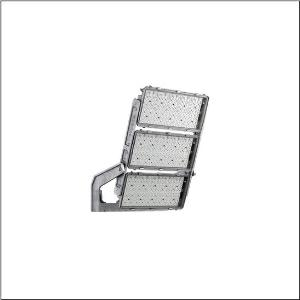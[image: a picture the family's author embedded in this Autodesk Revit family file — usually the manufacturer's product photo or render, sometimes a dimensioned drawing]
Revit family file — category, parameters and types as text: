
# Revit family: floodlight_fl_11_maxi_pro_remote___pl52_5xa779426d01aa_14f9
name_source: partatom
category: Lighting Fixtures
units: mm (PartAtom-declared; Revit-internal decimal feet)

## family parameters
Cut with Voids When Loaded = No
Host = Face
Light Source = No
Part Type = Normal
Room Calculation Point = No
Round Connector Dimension = Use Diameter
Shared = No

## types (1)
- --- (1 x LED, 169140 lm, 1387.6 W, 4000K)
    Apparent Load = 1388 VA
    CIE Flux Codes = 24 55 98 100 100
    Color Rendering = 70
    Color Temperature = 4000K
    Default Elevation = 1800 mm
    Description = Floodlight FL 11  maxi  pro Remote floodlight; light control with lens of PMMA; cover panel of toughened safety glass, transparent; light distribution: PL52, asymmetric direct distribution, LEDcolour temperature: 4000K, rated luminous flux: 169.140lm, colour rendering: CRI > 70, light colour: 740; luminous efficacy: 122lm/W; brightness control: DALI 2 (1 DALI address); with terminal, 8-pole, max. 2.5mm², mains connection: 220..240V/380..400V AC, 50/60Hz, surge voltage resistance: line to ground: 10kV, ECG replaceable separately, LED unit replaceable without ESD environment, dustproof LED module, dimming range 10..100%, no afterglow with DALI off / DMX off command; 1388W floodlight with 3x LED unit of diecast aluminium, coated grey; length: 713mm / width: 651mm / height: 338mm; mounting bracket, of diecast aluminium, uncoated, natural, equipment: Power, protection rating (complete): IP66; insulation class (complete): insulation class I (protective earthing); certification: CE, ENEC, VDE; ball protection: ball impact resistance with accessories, impact resistance: IK07; rated ambient temperature 10°C, only for outdoor installations, permissible operating ambient temperature: -40..+30°C, permissible storage temperature: -40..+85°C; packaging unit: 1 piece

Light Distribution: PL52
    Height = 320 mm
    Lamp = 1 x LED
    Lamp Light Flux = 169140 lm
    Lamp Power = 1387.6 W
    Lamp count = 1
    Length = 1002 mm
    Luminous efficacy = 122 lm/W
    Manufacturer = Siteco
    ModVariant = No
    Model = 5XA779426D01AA
    Mounting Place = Ceiling
    Mounting Type = Surface mounted
    Number of Poles = 1
    OnlyDefault = Yes
    Power Factor = 1
    Product Name = Floodlight FL 11 maxi pro Remote | PL52
    Product group = floodlight | ceiling mounted
    ProductGroupID = 302
    Protection Class = Protection class I
    Protection Degree = IP 66
    RLX_Detail_Level = 1
    RLX_Emergency_Light_Flux = 0 lm
    RLX_Emergency_Type = 0
    RLX_Emergency_Type_DB = No
    RlxData = <blob elided: 52421 chars, md5=a9be0326>
    Socket = socket
    Standby Power = 0 W
    System Light Flux = 169140 lm
    System Power = 1388 W
    Type Comments = factory setting: luminous flux: 100 % | dim-lin: 254 | 955 mA
    Type Image = l_1006784.jpg
    URL = http://relux.com
    VarID = @adj_028191
    Voltage = 0 V
    Weight = 0.00 kg
    Width = 655 mm

## geometry (parser evidence)
native form markers: Blend x4, Sweep x13
no freeform markers — native parametric forms only
